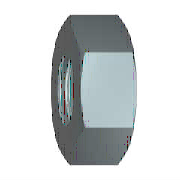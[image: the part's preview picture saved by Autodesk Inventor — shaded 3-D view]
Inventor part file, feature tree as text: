
AUTODESK INVENTOR PART (.ipt)
format: ipt  version: 2023.1 (Build 271208000, 208)  size: 164,352 bytes
history: native  units: mm (DEFAULTED — no unit token found)
features: sketch x3, chamfer x1, hole x1, other x1, plane x1
ambient origin geometry x7: Origin, YZ Plane, XZ Plane, X Axis, Y Axis, Z Axis, Center Point
bodies: Solid1 (feature_tree), Body (feature_tree)
feature tree (7):
  chamfer  "Chamfer1"  Angle=30.0deg  [1 undecoded]
  hole  "Thread"  [1 undecoded]
  other  "Work Axis1"
  plane  "Work Plane1"
  sketch  "Sketch1"  dims[d0=31.176915mm]
  sketch  "Sketch2"  dims[d1=17.6mm]
  sketch  "Sketch3"  dims[d2=0.0mm d3=30.0deg d4=30.0deg d5=24.85mm d6=24.85mm d7=90.0deg d25=16.376mm d26=6.0mm d27=4.0mm d28=2.0mm d29=14.3117mm d30=8.0mm d31=20.594885mm d8=0.811899mm d9=30.0deg d10=0.811899mm d11=30.0deg d13=0.0mm d14=0.0mm d39=0.0mm d40=0.811899mm d41=0.811899mm d42=0.0mm]
note: 2 required parameter values undecoded (feature->parameter linkage not recoverable at this tier; creation-order binding heuristic only, values carry confidence <= 0.55)
